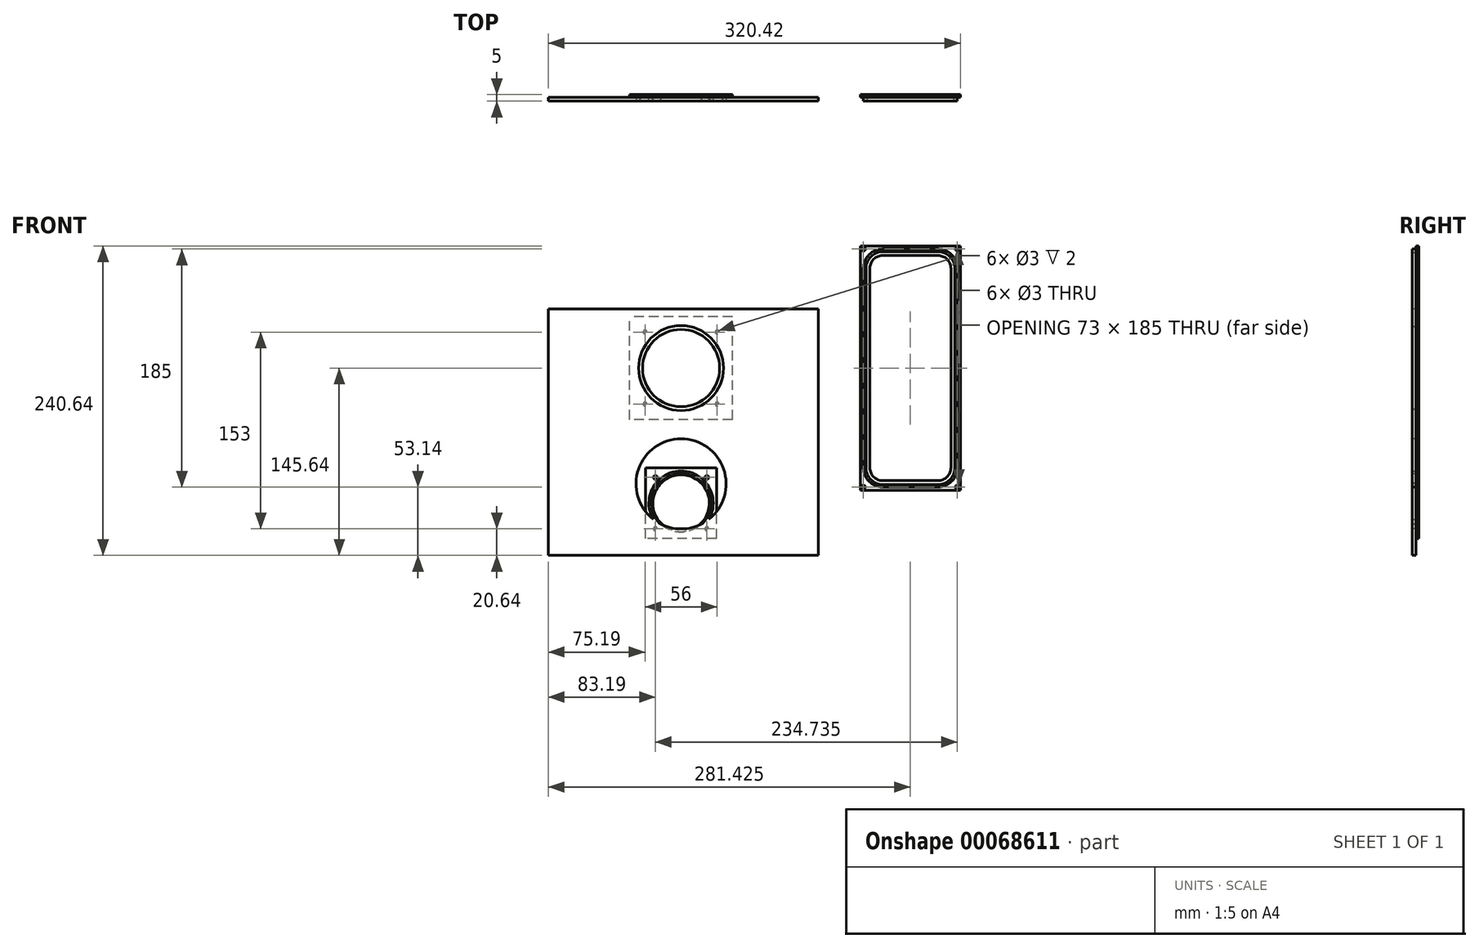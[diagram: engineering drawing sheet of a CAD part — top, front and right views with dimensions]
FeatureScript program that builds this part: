
annotation { "Feature Type Name" : "Feature", "Feature Type Description" : "" }
export const myFeature = defineFeature(function(context is Context, id is Id, definition is map)
    precondition{}
    {
        {
            var Q0;
            Q0=qCreatedBy(makeId("Front.planeOp"),FACE);
            cPlane(context, id + "F0", {"entities" : qUnion([Q0]), "cplaneType" : CPlaneType.OFFSET, "offset" : 5 * mm, "width" : 150 * mm, "height" : 150 * mm});
        }
        {
            var Q0;
            Q0=qCreatedBy(id+"F0.planeOp",FACE);
            var sketch = newSketch(context, id + "F1", { "sketchPlane" : qUnion([Q0])});
            skCircle(sketch, "E0", {"center": v(0, 0) * mm, "radius": 35 * mm});
            skCircle(sketch, "E1", {"center": v(0, -90) * mm, "radius": 35 * mm});
            skLineSegment(sketch, "E2.bottom", {"start": v(-103.2, 46.1) * mm, "end": v(106.7, 46.1) * mm});
            skLineSegment(sketch, "E2.top", {"start": v(-103.2, -145.64) * mm, "end": v(106.7, -145.64) * mm});
            skLineSegment(sketch, "E2.left", {"start": v(-103.2, 46.1) * mm, "end": v(-103.2, -145.64) * mm});
            skLineSegment(sketch, "E2.right", {"start": v(106.7, 46.1) * mm, "end": v(106.7, -145.64) * mm});
            skSolve(sketch);
        }
        {
            var Q0;
            Q0 = qSketchRegion(id + "F1", true);
            extrude(context, id + "F2", {"entities" : qUnion([Q0]), "oppositeDirection" : true, "depth" : 3 * mm});
        }
        {
            var Q0;
            Q0=qCreatedBy(makeId("Right.planeOp"),FACE);
            var sketch = newSketch(context, id + "F3", { "sketchPlane" : qUnion([Q0])});
            skLineSegment(sketch, "E3", {"start": v(19.32, 0) * mm, "end": v(-16.11, 0) * mm, "construction": true});
            skLineSegment(sketch, "E4", {"start": v(-5, 35) * mm, "end": v(-5, 33) * mm});
            skLineSegment(sketch, "E5", {"start": v(-5, 33) * mm, "end": v(0, 30) * mm});
            skLineSegment(sketch, "E6", {"start": v(0, 30) * mm, "end": v(0, 35) * mm});
            skLineSegment(sketch, "E7", {"start": v(0, 35) * mm, "end": v(-5, 35) * mm});
            skSolve(sketch);
        }
        {
            var Q0;
            Q0 = qSketchRegion(id + "F3", true);
            var Q1;
            Q1=sQuery(id+"F3.wireOp",EDGE,"E3");
            revolve(context, id + "F4", {"entities" : qUnion([Q0]), "axis" : qUnion([Q1]), "revolveType" : RevolveType.FULL});
        }
        {
            var Q0;
            Q0=qCreatedBy(makeId("Front.planeOp"),FACE);
            var sketch = newSketch(context, id + "F5", { "sketchPlane" : qUnion([Q0])});
            skCircle(sketch, "E8", {"center": v(0, 0) * mm, "radius": 35 * mm});
            skLineSegment(sketch, "E9.bottom", {"start": v(40, -40) * mm, "end": v(-40, -40) * mm});
            skLineSegment(sketch, "E9.top", {"start": v(40, 40) * mm, "end": v(-40, 40) * mm});
            skLineSegment(sketch, "E9.left", {"start": v(40, -40) * mm, "end": v(40, 40) * mm});
            skLineSegment(sketch, "E9.right", {"start": v(-40, -40) * mm, "end": v(-40, 40) * mm});
            skCircle(sketch, "E10", {"center": v(-28, 28) * mm, "radius": 1.5 * mm});
            skCircle(sketch, "E11", {"center": v(-28, -28) * mm, "radius": 1.5 * mm});
            skCircle(sketch, "E12", {"center": v(28, 28) * mm, "radius": 1.5 * mm});
            skCircle(sketch, "E13", {"center": v(28, -28) * mm, "radius": 1.5 * mm});
            skSolve(sketch);
        }
        {
            var Q0;
            Q0 = qSketchRegion(id + "F5", true);
            extrude(context, id + "F6", {"entities" : qUnion([Q0]), "operationType" : NewBodyOperationType.ADD, "depth" : 2 * mm});
        }
        {
            var Q0;
            Q0=qCreatedBy(makeId("Front.planeOp"),FACE);
            var sketch = newSketch(context, id + "F7", { "sketchPlane" : qUnion([Q0])});
            skLineSegment(sketch, "E14.bottom", {"start": v(217.23, -95) * mm, "end": v(139.23, -95) * mm});
            skLineSegment(sketch, "E14.top", {"start": v(217.23, 95) * mm, "end": v(139.23, 95) * mm});
            skLineSegment(sketch, "E14.left", {"start": v(217.23, -95) * mm, "end": v(217.23, 95) * mm});
            skLineSegment(sketch, "E14.right", {"start": v(139.23, -95) * mm, "end": v(139.23, 95) * mm});
            skPoint(sketch, "E14.middle", {"position": v(178.23, 0) * mm});
            skLineSegment(sketch, "E15.bottom", {"start": v(199.73, -92.5) * mm, "end": v(156.73, -92.5) * mm});
            skLineSegment(sketch, "E15.top", {"start": v(199.73, 92.5) * mm, "end": v(156.73, 92.5) * mm});
            skLineSegment(sketch, "E15.left", {"start": v(214.73, -77.5) * mm, "end": v(214.73, 77.5) * mm});
            skLineSegment(sketch, "E15.right", {"start": v(141.73, -77.5) * mm, "end": v(141.73, 77.5) * mm});
            skPoint(sketch, "E16.visualSharp", {"position": v(141.73, 92.5) * mm});
            skArc(sketch, "E16.filletArc", {"start": v(156.73, 92.5) * mm, "mid": v(146.13, 88.1) * mm, "end": v(141.73, 77.5) * mm});
            skPoint(sketch, "E17.visualSharp", {"position": v(214.73, 92.5) * mm});
            skArc(sketch, "E17.filletArc", {"start": v(214.73, 77.5) * mm, "mid": v(210.34, 88.1) * mm, "end": v(199.73, 92.5) * mm});
            skPoint(sketch, "E18.visualSharp", {"position": v(141.73, -92.5) * mm});
            skArc(sketch, "E18.filletArc", {"start": v(141.73, -77.5) * mm, "mid": v(146.13, -88.1) * mm, "end": v(156.73, -92.5) * mm});
            skPoint(sketch, "E19.visualSharp", {"position": v(214.73, -92.5) * mm});
            skArc(sketch, "E19.filletArc", {"start": v(199.73, -92.5) * mm, "mid": v(210.34, -88.1) * mm, "end": v(214.73, -77.5) * mm});
            skCircle(sketch, "E20", {"center": v(141.73, 92.5) * mm, "radius": 1.5 * mm});
            skCircle(sketch, "E21", {"center": v(214.73, 92.5) * mm, "radius": 1.5 * mm});
            skCircle(sketch, "E22", {"center": v(141.73, -92.5) * mm, "radius": 1.5 * mm});
            skCircle(sketch, "E23", {"center": v(214.73, -92.5) * mm, "radius": 1.5 * mm});
            skSolve(sketch);
        }
        {
            var Q0;
            Q0=makeQuery(id+"F7.imprint","IMPRINT",FACE,{"disambiguationData":[TD([[makeQuery(id+"F7.imprint","IMPRINT",EDGE,{"derivedFrom":sQuery(id+"F7.wireOp",EDGE,"E14.bottom")}),-1.0]])]});
            extrude(context, id + "F8", {"entities" : qUnion([Q0]), "depth" : 2 * mm});
        }
        {
            var Q0;
            Q0=qCreatedBy(makeId("Top.planeOp"),FACE);
            cPlane(context, id + "F9", {"entities" : qUnion([Q0]), "cplaneType" : CPlaneType.OFFSET, "offset" : 77.5 * mm, "oppositeDirection" : true, "width" : 150 * mm, "height" : 150 * mm});
        }
        {
            var Q0;
            Q0=qCreatedBy(id+"F9.planeOp",FACE);
            var sketch = newSketch(context, id + "F10", { "sketchPlane" : qUnion([Q0])});
            skLineSegment(sketch, "E24", {"start": v(141.74, -5) * mm, "end": v(141.74, 0) * mm});
            skLineSegment(sketch, "E25", {"start": v(141.74, 0) * mm, "end": v(146.74, 0) * mm});
            skLineSegment(sketch, "E26", {"start": v(146.74, 0) * mm, "end": v(143.74, -5) * mm});
            skLineSegment(sketch, "E27", {"start": v(143.74, -5) * mm, "end": v(141.74, -5) * mm});
            skSolve(sketch);
        }
        {
            var Q0;
            Q0 = qSketchRegion(id + "F10", true);
            var Q1;
            Q1=sQuery(id+"F7.wireOp",EDGE,"E15.right");
            var Q2;
            Q2=sQuery(id+"F7.wireOp",EDGE,"E16.filletArc");
            var Q3;
            Q3=sQuery(id+"F7.wireOp",EDGE,"E15.top");
            var Q4;
            Q4=sQuery(id+"F7.wireOp",EDGE,"E17.filletArc");
            var Q5;
            Q5=sQuery(id+"F7.wireOp",EDGE,"E15.left");
            var Q6;
            Q6=sQuery(id+"F7.wireOp",EDGE,"E19.filletArc");
            var Q7;
            Q7=sQuery(id+"F7.wireOp",EDGE,"E15.bottom");
            var Q8;
            Q8=sQuery(id+"F7.wireOp",EDGE,"E18.filletArc");
            sweep(context, id + "F11", {"operationType" : NewBodyOperationType.ADD, "profiles" : qUnion([Q0]), "path" : qUnion([Q1, Q2, Q3, Q4, Q5, Q6, Q7, Q8])});
        }
        {
            var Q0;
            Q0=qCreatedBy(makeId("Right.planeOp"),FACE);
            var sketch = newSketch(context, id + "F12", { "sketchPlane" : qUnion([Q0])});
            skLineSegment(sketch, "E28", {"start": v(19.32, -105) * mm, "end": v(-16.11, -105) * mm, "construction": true});
            skLineSegment(sketch, "E29", {"start": v(-5, -80) * mm, "end": v(-5, -82) * mm});
            skLineSegment(sketch, "E30", {"start": v(-5, -82) * mm, "end": v(0, -83) * mm});
            skLineSegment(sketch, "E31", {"start": v(0, -83) * mm, "end": v(0, -80) * mm});
            skLineSegment(sketch, "E32", {"start": v(0, -80) * mm, "end": v(-5, -80) * mm});
            skSolve(sketch);
        }
        {
            var Q0;
            Q0=makeQuery(id+"F12.imprint","IMPRINT",FACE,{"disambiguationData":[TD([[makeQuery(id+"F12.imprint","IMPRINT",EDGE,{"derivedFrom":sQuery(id+"F12.wireOp",EDGE,"E29")}),1.0]])]});
            var Q1;
            Q1=sQuery(id+"F12.wireOp",EDGE,"E28");
            revolve(context, id + "F13", {"entities" : qUnion([Q0]), "axis" : qUnion([Q1]), "revolveType" : RevolveType.FULL});
        }
        {
            var Q0;
            Q0=qCreatedBy(makeId("Front.planeOp"),FACE);
            var sketch = newSketch(context, id + "F14", { "sketchPlane" : qUnion([Q0])});
            skCircle(sketch, "E33", {"center": v(0, -105) * mm, "radius": 25 * mm});
            skLineSegment(sketch, "E34.bottom", {"start": v(27.5, -132.5) * mm, "end": v(-27.5, -132.5) * mm});
            skLineSegment(sketch, "E34.top", {"start": v(27.5, -77.5) * mm, "end": v(-27.5, -77.5) * mm});
            skLineSegment(sketch, "E34.left", {"start": v(27.5, -132.5) * mm, "end": v(27.5, -77.5) * mm});
            skLineSegment(sketch, "E34.right", {"start": v(-27.5, -132.5) * mm, "end": v(-27.5, -77.5) * mm});
            skCircle(sketch, "E35", {"center": v(-20, -85) * mm, "radius": 1.5 * mm});
            skCircle(sketch, "E36", {"center": v(-20, -125) * mm, "radius": 1.5 * mm});
            skCircle(sketch, "E37", {"center": v(20, -85) * mm, "radius": 1.5 * mm});
            skCircle(sketch, "E38", {"center": v(20, -125) * mm, "radius": 1.5 * mm});
            skSolve(sketch);
        }
        {
            var Q0;
            Q0 = qSketchRegion(id + "F14", true);
            extrude(context, id + "F15", {"entities" : qUnion([Q0]), "operationType" : NewBodyOperationType.ADD, "depth" : 2 * mm});
        }
    });
